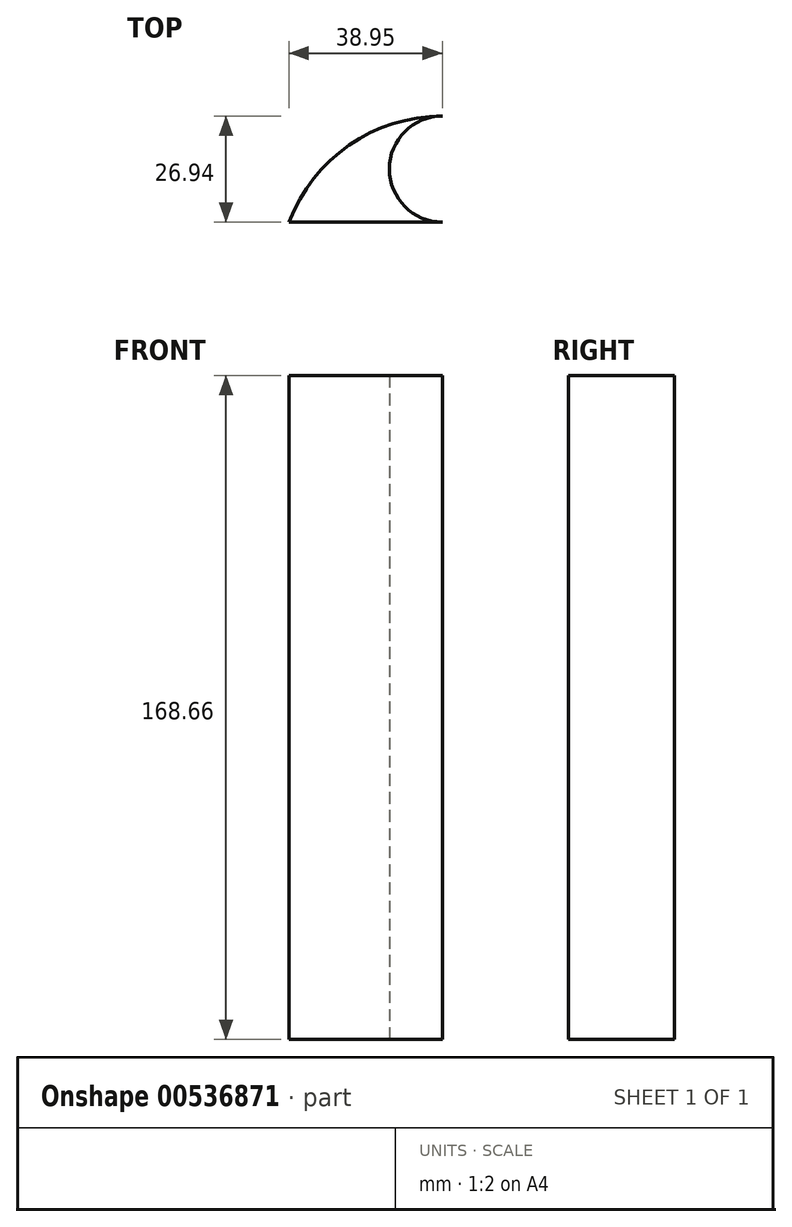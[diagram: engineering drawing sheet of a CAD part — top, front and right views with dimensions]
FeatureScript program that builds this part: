
annotation { "Feature Type Name" : "Feature", "Feature Type Description" : "" }
export const myFeature = defineFeature(function(context is Context, id is Id, definition is map)
    precondition{}
    {
        {
            var Q0;
            Q0=qCreatedBy(makeId("Top.planeOp"),FACE);
            var sketch = newSketch(context, id + "F0", { "sketchPlane" : qUnion([Q0])});
            skLineSegment(sketch, "E0.bottom", {"start": v(0, 0) * mm, "end": v(-38.95, 0) * mm});
            skLineSegment(sketch, "E0.top", {"start": v(0, 26.94) * mm, "end": v(-38.95, 26.94) * mm});
            skLineSegment(sketch, "E0.left", {"start": v(0, 0) * mm, "end": v(0, 26.94) * mm});
            skLineSegment(sketch, "E0.right", {"start": v(-38.95, 0) * mm, "end": v(-38.95, 26.94) * mm});
            skPoint(sketch, "E1.oppositeSnap0", {"position": v(-19.47, 26.94) * mm});
            skLineSegment(sketch, "E1.bottom", {"start": v(-33.5, 26.94) * mm, "end": v(-19.47, 26.94) * mm});
            skLineSegment(sketch, "E1.top", {"start": v(-33.5, 43.08) * mm, "end": v(-19.47, 43.08) * mm});
            skLineSegment(sketch, "E1.left", {"start": v(-33.5, 26.94) * mm, "end": v(-33.5, 43.08) * mm});
            skLineSegment(sketch, "E1.right", {"start": v(-19.47, 26.94) * mm, "end": v(-19.47, 43.08) * mm});
            skArc(sketch, "E2", {"start": v(0, 26.94) * mm, "mid": v(-13.47, 13.47) * mm, "end": v(0, 0) * mm});
            skArc(sketch, "E3", {"start": v(0, 26.94) * mm, "mid": v(-23.68, 19.55) * mm, "end": v(-38.95, 0) * mm});
            skSolve(sketch);
        }
        {
            var Q0;
            Q0=makeQuery(id+"F0.imprint","IMPRINT",FACE,{"disambiguationData":[TD([[makeQuery(id+"F0.imprint","IMPRINT",EDGE,{"derivedFrom":sQuery(id+"F0.wireOp",EDGE,"E1.bottom")}),1.0]])]});
            var Q1;
            Q1=makeQuery(id+"F0.imprint","IMPRINT",FACE,{"disambiguationData":[TD([[makeQuery(id+"F0.imprint","IMPRINT",EDGE,{"derivedFrom":sQuery(id+"F0.wireOp",EDGE,"E0.bottom")}),-1.0]])]});
            extrude(context, id + "F1", {"entities" : qUnion([Q0, Q1]), "depth" : 168.66 * mm, "offsetDistance" : 25.4 * mm});
        }
        {
            var Q0;
            Q0=qCreatedBy(makeId("Top.planeOp"),FACE);
            var sketch = newSketch(context, id + "F2", { "sketchPlane" : qUnion([Q0])});
            skCircle(sketch, "E4", {"center": v(-18.2, 22.44) * mm, "radius": 4.26 * mm});
            skSolve(sketch);
        }
        {
            var Q0;
            Q0 = qSketchRegion(id + "F2", true);
            extrude(context, id + "F3", {"entities" : qUnion([Q0]), "operationType" : NewBodyOperationType.REMOVE, "oppositeDirection" : true, "depth" : 89.15 * mm, "offsetDistance" : 25.4 * mm});
        }
        {
            var Q0;
            Q0=makeQuery(id+"F1.opExtrude","CAP_FACE",FACE,{"disambiguationData":[OSD([sQuery(id+"F0.wireOp",EDGE,"E0.bottom"),sQuery(id+"F0.wireOp",EDGE,"E2"),sQuery(id+"F0.wireOp",EDGE,"E3")])],"isStart":false});
            extrude(context, id + "F4", {"entities" : qUnion([Q0]), "operationType" : NewBodyOperationType.REMOVE, "depth" : 25.4 * mm, "offsetDistance" : 25.4 * mm});
        }
    });
